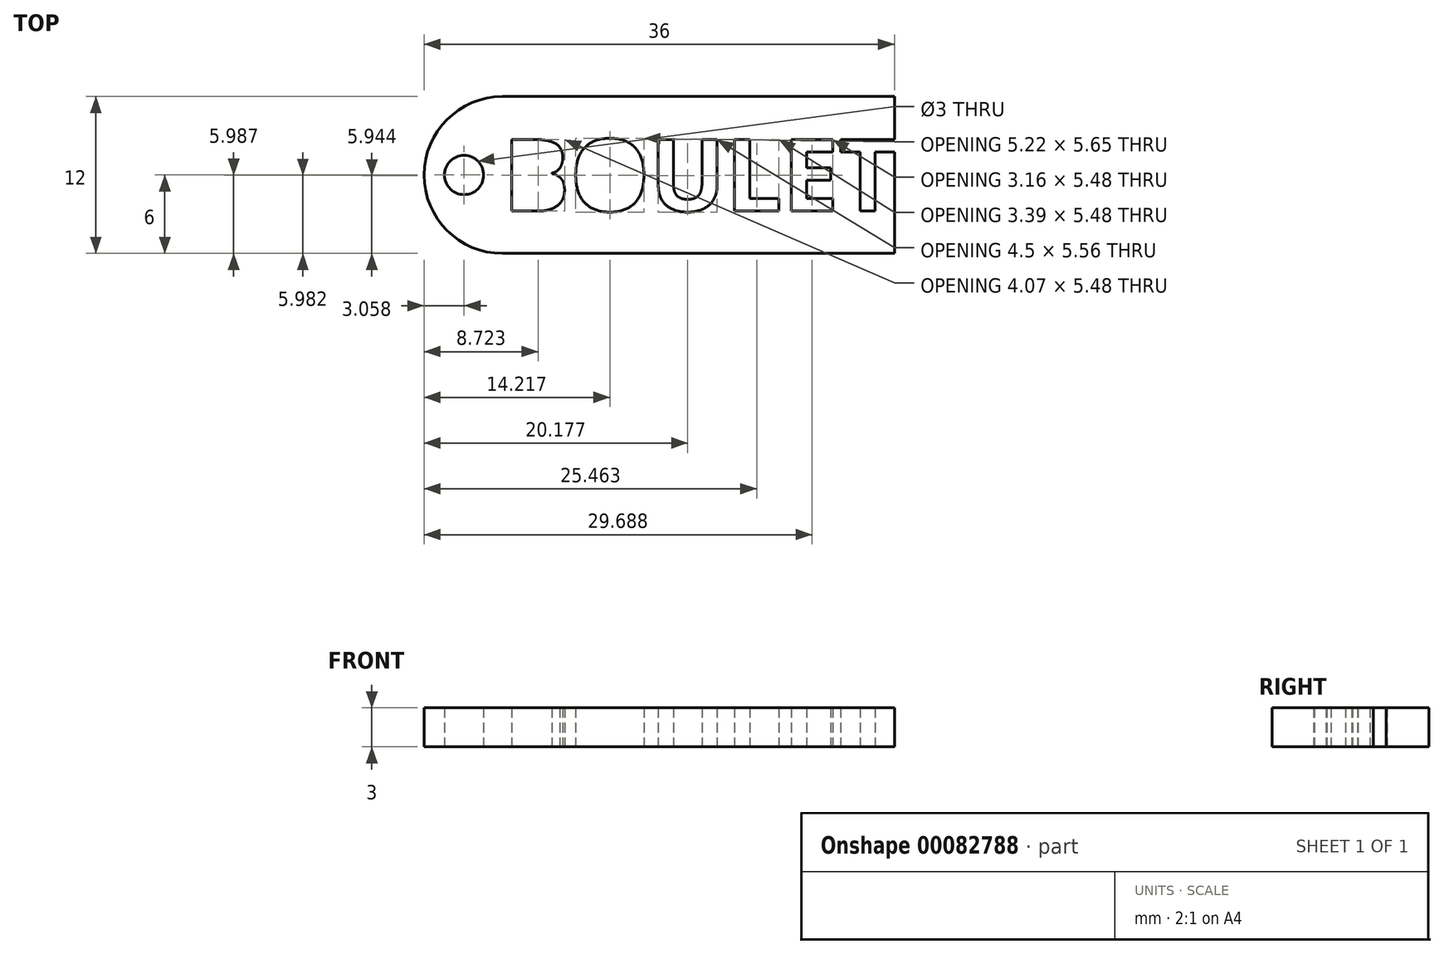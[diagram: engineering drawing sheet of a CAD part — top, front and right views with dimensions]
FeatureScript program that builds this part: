
annotation { "Feature Type Name" : "Feature", "Feature Type Description" : "" }
export const myFeature = defineFeature(function(context is Context, id is Id, definition is map)
    precondition{}
    {
        {
            var Q0;
            Q0=qCreatedBy(makeId("Top.planeOp"),FACE);
            var sketch = newSketch(context, id + "F0", { "sketchPlane" : qUnion([Q0])});
            skLineSegment(sketch, "E0.bottom", {"start": v(-15, 6) * mm, "end": v(15, 6) * mm});
            skLineSegment(sketch, "E0.top", {"start": v(-15, -6) * mm, "end": v(15, -6) * mm});
            skLineSegment(sketch, "E0.left", {"start": v(-15, 6) * mm, "end": v(-15, -6) * mm});
            skLineSegment(sketch, "E0.right", {"start": v(15, 6) * mm, "end": v(15, -6) * mm});
            skPoint(sketch, "E0.middle", {"position": v(0, 0) * mm});
            skArc(sketch, "E1", {"start": v(-15, 6) * mm, "mid": v(-21, 0) * mm, "end": v(-15, -6) * mm});
            skArc(sketch, "E2", {"start": v(15, 6) * mm, "mid": v(21, 0) * mm, "end": v(15, -6) * mm});
            skText(sketch, "E3", { "text": "BOULET", "fontName": "OpenSans-Bold.ttf"});
            skCircle(sketch, "E4", {"center": v(-17.94, 0) * mm, "radius": 1.5 * mm});
            const initialGuessF0  = {"E3": [-0.015, -0.00276, 1, 0, 0.00553]};
            skSetInitialGuess(sketch, initialGuessF0);
            skSolve(sketch);
        }
        {
            var Q0;
            Q0=makeQuery(id+"F0.imprint","IMPRINT",FACE,{"disambiguationData":[TD([[makeQuery(id+"F0.imprint","IMPRINT",EDGE,{"derivedFrom":sQuery(id+"F0.wireOp",EDGE,"E0.left")}),-1.0]])]});
            var Q1;
            {var subQ1=sQuery(id+"F0.wireOp",EDGE,"E0.bottom");Q1=makeQuery(id+"F0.imprint","IMPRINT",FACE,{"disambiguationData":[TD([[makeQuery(id+"F0.imprint","IMPRINT",EDGE,{"derivedFrom":subQ1}),-1.0]])]});}
            var Q2;
            {var subQ0=sQuery(id+"F0.wireOp",EDGE,"E2");Q2=makeQuery(id+"F0.imprint","IMPRINT",FACE,{"disambiguationData":[TD([[makeQuery(id+"F0.imprint","IMPRINT",EDGE,{"derivedFrom":subQ0}),-1.0]])]});}
            extrude(context, id + "F1", {"entities" : qUnion([Q0, Q1, Q2]), "depth" : 3 * mm});
        }
    });
